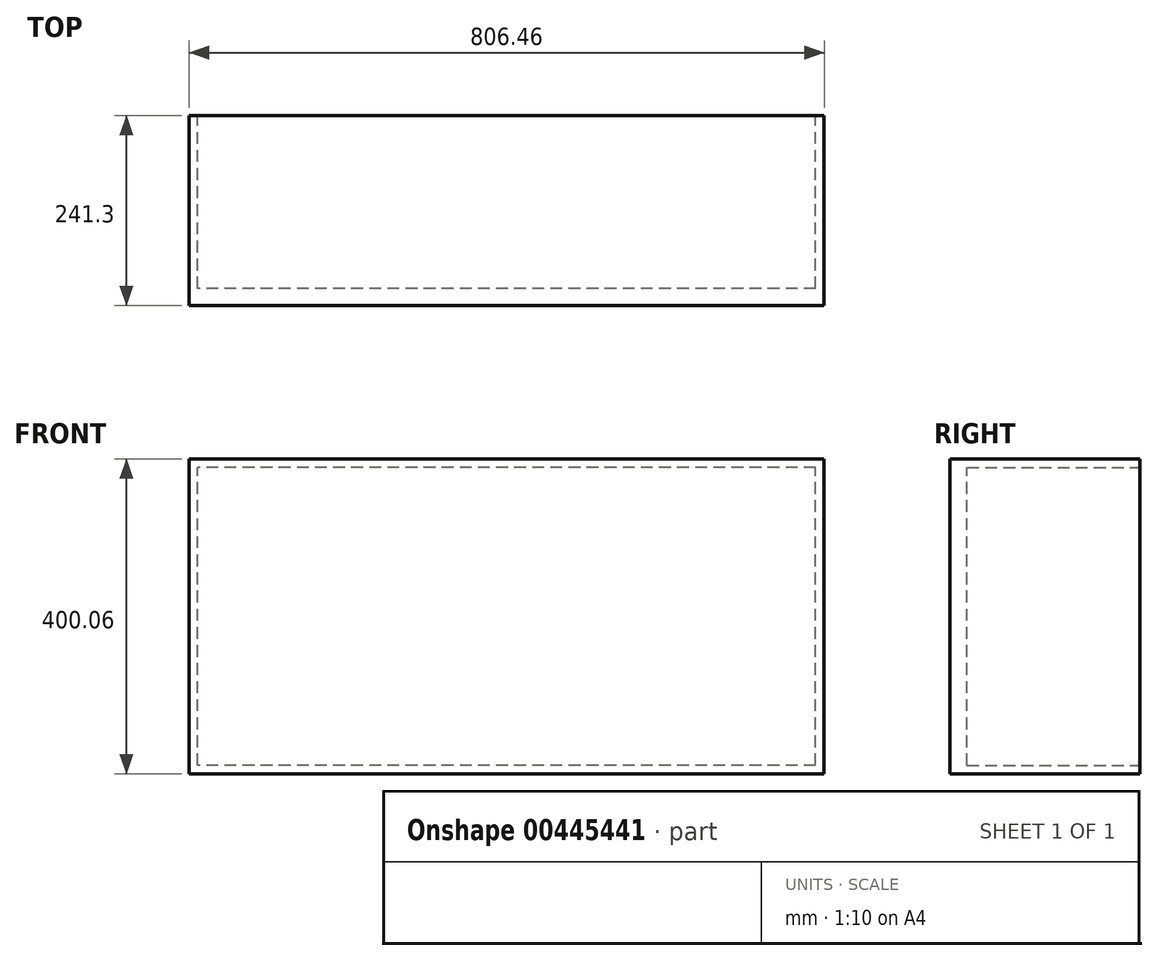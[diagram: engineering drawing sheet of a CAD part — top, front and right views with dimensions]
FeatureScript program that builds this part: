
annotation { "Feature Type Name" : "Feature", "Feature Type Description" : "" }
export const myFeature = defineFeature(function(context is Context, id is Id, definition is map)
    precondition{}
    {
        {
            var Q0;
            Q0=qCreatedBy(makeId("Front.planeOp"),FACE);
            var sketch = newSketch(context, id + "F0", { "sketchPlane" : qUnion([Q0])});
            skLineSegment(sketch, "E0.bottom", {"start": v(403.23, 200.03) * mm, "end": v(-403.23, 200.03) * mm});
            skLineSegment(sketch, "E0.top", {"start": v(403.23, -200.03) * mm, "end": v(-403.23, -200.03) * mm});
            skLineSegment(sketch, "E0.left", {"start": v(403.23, 200.03) * mm, "end": v(403.23, -200.03) * mm});
            skLineSegment(sketch, "E0.right", {"start": v(-403.23, 200.03) * mm, "end": v(-403.23, -200.03) * mm});
            skPoint(sketch, "E0.middle", {"position": v(0, 0) * mm});
            skSolve(sketch);
        }
        {
            var Q0;
            Q0 = qSketchRegion(id + "F0", true);
            extrude(context, id + "F1", {"entities" : qUnion([Q0]), "depth" : 241.3 * mm});
        }
        {
            var Q0;
            Q0=makeQuery(id+"F1.opExtrude","CAP_FACE",FACE,{"disambiguationData":[OSD([sQuery(id+"F0.wireOp",EDGE,"E0.bottom"),sQuery(id+"F0.wireOp",EDGE,"E0.top"),sQuery(id+"F0.wireOp",EDGE,"E0.left"),sQuery(id+"F0.wireOp",EDGE,"E0.right")])],"isStart":true});
            var sketch = newSketch(context, id + "F2", { "sketchPlane" : qUnion([Q0])});
            skLineSegment(sketch, "E1.bottom", {"start": v(-392.43, -189.23) * mm, "end": v(392.43, -189.23) * mm});
            skLineSegment(sketch, "E1.top", {"start": v(-392.43, 189.23) * mm, "end": v(392.43, 189.23) * mm});
            skLineSegment(sketch, "E1.left", {"start": v(-392.43, -189.23) * mm, "end": v(-392.43, 189.23) * mm});
            skLineSegment(sketch, "E1.right", {"start": v(392.43, -189.23) * mm, "end": v(392.43, 189.23) * mm});
            skPoint(sketch, "E1.middle", {"position": v(0, 0) * mm});
            skSolve(sketch);
        }
        {
            var Q0;
            Q0=makeQuery(id+"F2.imprint","IMPRINT",FACE,{"disambiguationData":[TD([[makeQuery(id+"F2.imprint","IMPRINT",EDGE,{"derivedFrom":sQuery(id+"F2.wireOp",EDGE,"E1.bottom")}),1.0]])]});
            extrude(context, id + "F3", {"entities" : qUnion([Q0]), "operationType" : NewBodyOperationType.REMOVE, "oppositeDirection" : true, "depth" : 219.71 * mm});
        }
    });
